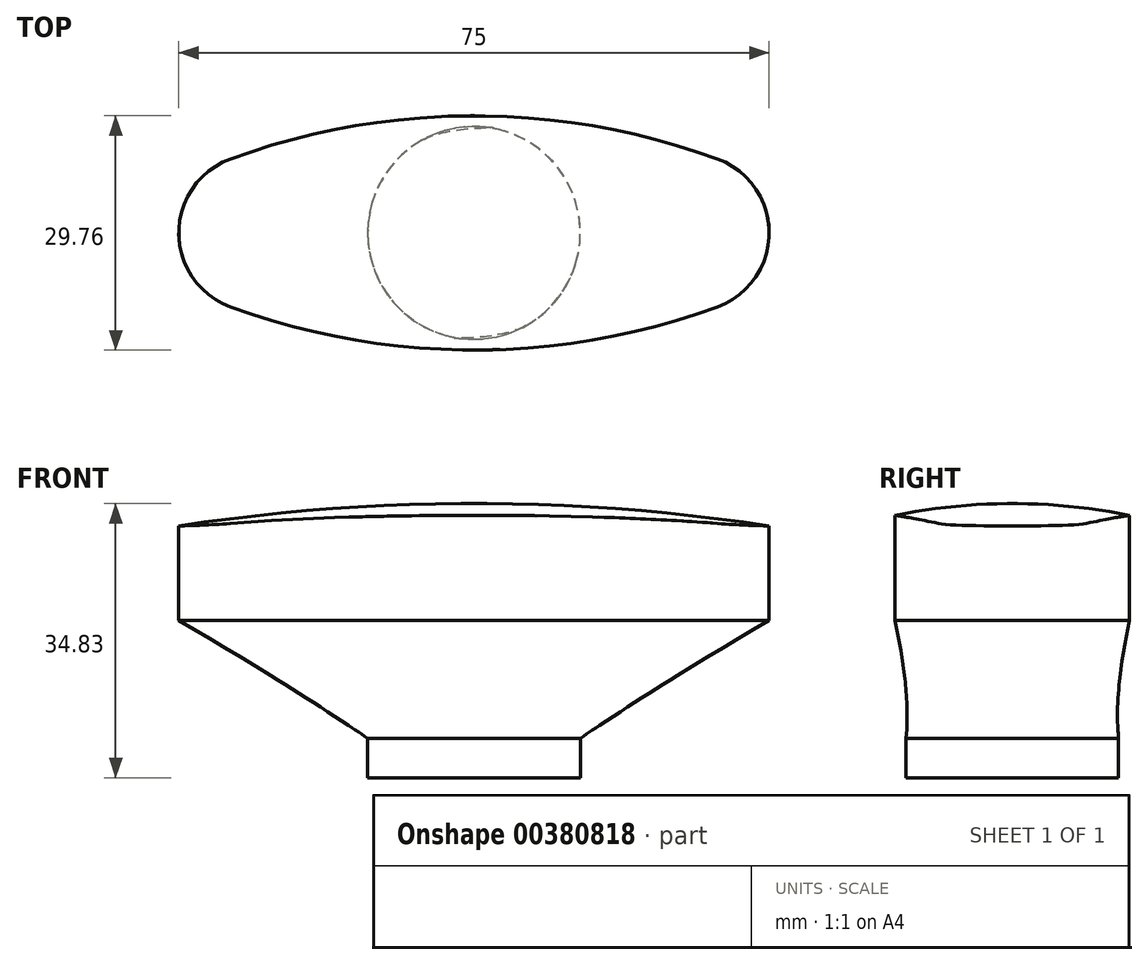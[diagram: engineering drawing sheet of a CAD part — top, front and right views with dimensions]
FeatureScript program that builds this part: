
annotation { "Feature Type Name" : "Feature", "Feature Type Description" : "" }
export const myFeature = defineFeature(function(context is Context, id is Id, definition is map)
    precondition{}
    {
        {
            var Q0;
            Q0=qCreatedBy(makeId("Top.planeOp"),FACE);
            var sketch = newSketch(context, id + "F0", { "sketchPlane" : qUnion([Q0])});
            skArc(sketch, "E0", {"start": v(-30.94, 9.4) * mm, "mid": v(-37.5, 0) * mm, "end": v(-30.94, -9.4) * mm});
            skArc(sketch, "E1", {"start": v(-30.94, 9.4) * mm, "mid": v(0, 14.88) * mm, "end": v(30.94, 9.4) * mm});
            skArc(sketch, "E2", {"start": v(30.94, -9.4) * mm, "mid": v(0, -14.88) * mm, "end": v(-30.94, -9.4) * mm});
            skArc(sketch, "E3", {"start": v(30.94, 9.4) * mm, "mid": v(37.5, 0) * mm, "end": v(30.94, -9.4) * mm});
            skLineSegment(sketch, "E4", {"start": v(-27.5, 0) * mm, "end": v(27.5, 0) * mm, "construction": true});
            skSolve(sketch);
        }
        {
            var Q0;
            Q0=qCreatedBy(makeId("Front.planeOp"),FACE);
            var sketch = newSketch(context, id + "F1", { "sketchPlane" : qUnion([Q0])});
            skArc(sketch, "E5", {"start": v(37.5, 0) * mm, "mid": v(0, 2.83) * mm, "end": v(-37.5, 0) * mm});
            skLineSegment(sketch, "E6", {"start": v(-37.97, -72.17) * mm, "end": v(32.46, -72.17) * mm, "construction": true});
            skSolve(sketch);
        }
        {
            var Q0;
            Q0 = qSketchRegion(id + "F1", true);
            var Q1;
            Q1=sQuery(id+"F1.wireOp",EDGE,"E5");
            var Q2;
            Q2=sQuery(id+"F1.wireOp",EDGE,"E6");
            revolve(context, id + "F2", {"bodyType" : ToolBodyType.SURFACE, "entities" : qUnion([Q0]), "surfaceEntities" : qUnion([Q1]), "axis" : qUnion([Q2]), "revolveType" : RevolveType.SYMMETRIC, "angle" : 180 * degree});
        }
        {
            var Q0;
            Q0 = qSketchRegion(id + "F0", true);
            var Q1;
            Q1=makeQuery(id+"F2.opRevolve","SWEPT_FACE",FACE,{"disambiguationData":[OSD([sQuery(id+"F1.wireOp",EDGE,"E5")])]});
            extrude(context, id + "F3", {"entities" : qUnion([Q0]), "endBound" : BoundingType.UP_TO_SURFACE, "endBoundEntityFace" : qUnion([Q1]), "depth" : 25 * mm, "hasSecondDirection" : true, "secondDirectionOppositeDirection" : true, "secondDirectionDepth" : 12 * mm});
        }
        {
            var Q0;
            Q0=makeQuery(id+"F3.opExtrude","CAP_FACE",FACE,{"disambiguationData":[OSD([sQuery(id+"F0.wireOp",EDGE,"E0"),sQuery(id+"F0.wireOp",EDGE,"E1"),sQuery(id+"F0.wireOp",EDGE,"E2"),sQuery(id+"F0.wireOp",EDGE,"E3")])],"isStart":true});
            cPlane(context, id + "F4", {"entities" : qUnion([Q0]), "cplaneType" : CPlaneType.OFFSET, "offset" : 15 * mm, "width" : 150 * mm, "height" : 150 * mm});
        }
        {
            var Q0;
            Q0=qCreatedBy(id+"F4.planeOp",FACE);
            var sketch = newSketch(context, id + "F5", { "sketchPlane" : qUnion([Q0])});
            skCircle(sketch, "E7", {"center": v(0, 0) * mm, "radius": 13.5 * mm});
            skSolve(sketch);
        }
        {
            var Q0;
            Q0=makeQuery(id+"F3.opExtrude","CAP_FACE",FACE,{"disambiguationData":[OSD([sQuery(id+"F0.wireOp",EDGE,"E0"),sQuery(id+"F0.wireOp",EDGE,"E1"),sQuery(id+"F0.wireOp",EDGE,"E2"),sQuery(id+"F0.wireOp",EDGE,"E3")])],"isStart":true});
            var Q1;
            Q1=makeQuery(id+"F5.imprint","IMPRINT",FACE,{"disambiguationData":[TD([[makeQuery(id+"F5.imprint","IMPRINT",EDGE,{"derivedFrom":sQuery(id+"F5.wireOp",EDGE,"E7")}),1.0]])]});
            loft(context, id + "F6", {"operationType" : NewBodyOperationType.ADD, "sheetProfilesArray" : [{ "sheetProfileEntities" : qUnion([Q0]) }, { "sheetProfileEntities" : qUnion([Q1]) }]});
        }
        {
            var Q0;
            Q0 = qSketchRegion(id + "F5", true);
            extrude(context, id + "F7", {"entities" : qUnion([Q0]), "operationType" : NewBodyOperationType.ADD, "depth" : 5 * mm});
        }
    });
